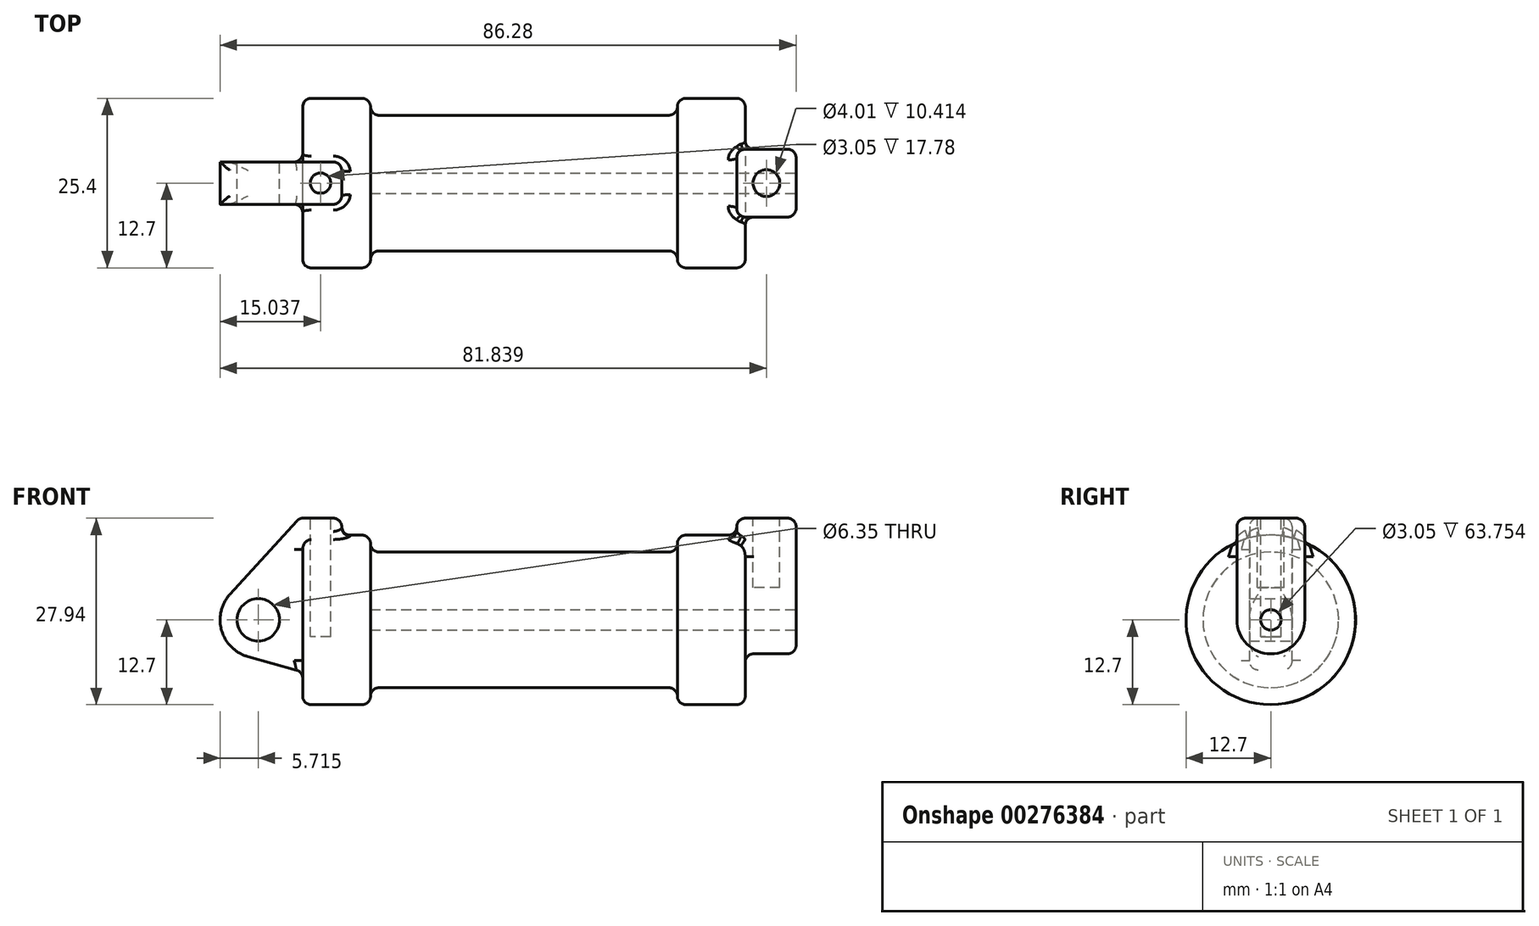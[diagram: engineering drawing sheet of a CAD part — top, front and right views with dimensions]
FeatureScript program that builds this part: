
annotation { "Feature Type Name" : "Feature", "Feature Type Description" : "" }
export const myFeature = defineFeature(function(context is Context, id is Id, definition is map)
    precondition{}
    {
        {
            var Q0;
            Q0=qCreatedBy(makeId("Front.planeOp"),FACE);
            var sketch = newSketch(context, id + "F0", { "sketchPlane" : qUnion([Q0])});
            skLineSegment(sketch, "E0", {"start": v(0, 0) * mm, "end": v(0, 12.7) * mm});
            skLineSegment(sketch, "E1", {"start": v(0, 12.7) * mm, "end": v(10.16, 12.7) * mm});
            skLineSegment(sketch, "E2", {"start": v(10.16, 12.7) * mm, "end": v(10.16, 10.16) * mm});
            skLineSegment(sketch, "E3", {"start": v(10.16, 10.16) * mm, "end": v(56.13, 10.16) * mm});
            skLineSegment(sketch, "E4", {"start": v(56.13, 10.16) * mm, "end": v(56.13, 12.7) * mm});
            skLineSegment(sketch, "E5", {"start": v(56.13, 12.7) * mm, "end": v(66.3, 12.7) * mm});
            skLineSegment(sketch, "E6", {"start": v(66.3, 12.7) * mm, "end": v(66.3, 0) * mm});
            skLineSegment(sketch, "E7", {"start": v(66.3, 0) * mm, "end": v(0, 0) * mm});
            skLineSegment(sketch, "E8", {"start": v(5.84, 15.24) * mm, "end": v(-0.5, 15.24) * mm});
            skLineSegment(sketch, "E9", {"start": v(-0.5, 15.24) * mm, "end": v(-10.88, 3.85) * mm});
            skLineSegment(sketch, "E10", {"start": v(0, 0) * mm, "end": v(-6.65, 0) * mm});
            skArc(sketch, "E11", {"start": v(-10.88, 3.85) * mm, "mid": v(-12.15, -1.58) * mm, "end": v(-8.18, -5.5) * mm});
            skCircle(sketch, "E12", {"center": v(-6.65, 0) * mm, "radius": 3.18 * mm});
            skLineSegment(sketch, "E13", {"start": v(5.84, 15.24) * mm, "end": v(5.84, -9.4) * mm});
            skLineSegment(sketch, "E14", {"start": v(5.84, -9.4) * mm, "end": v(-8.18, -5.5) * mm});
            skSolve(sketch);
        }
        {
            var Q0;
            {var subQ0=sQuery(id+"F0.wireOp",EDGE,"E2");Q0=makeQuery(id+"F0.imprint","IMPRINT",FACE,{"disambiguationData":[TD([[makeQuery(id+"F0.imprint","IMPRINT",EDGE,{"derivedFrom":subQ0}),-1.0]])]});}
            var Q1;
            {var subQ0=sQuery(id+"F0.wireOp",EDGE,"E0");Q1=makeQuery(id+"F0.imprint","IMPRINT",FACE,{"disambiguationData":[TD([[makeQuery(id+"F0.imprint","IMPRINT",EDGE,{"derivedFrom":subQ0}),-1.0]])]});}
            var Q2;
            Q2=sQuery(id+"F0.wireOp",EDGE,"E7");
            revolve(context, id + "F1", {"entities" : qUnion([Q0, Q1]), "axis" : qUnion([Q2]), "revolveType" : RevolveType.FULL});
        }
        {
            var Q0;
            {var subQ3=sQuery(id+"F0.wireOp",EDGE,"E0");Q0=makeQuery(id+"F0.imprint","IMPRINT",FACE,{"disambiguationData":[TD([[makeQuery(id+"F0.imprint","IMPRINT",EDGE,{"derivedFrom":subQ3}),1.0]])]});}
            var sketch = newSketch(context, id + "F2", { "sketchPlane" : qUnion([Q0])});
            skSolve(sketch);
        }
        {
            var Q0;
            {var subQ3=sQuery(id+"F0.wireOp",EDGE,"E0");Q0=makeQuery(id+"F2.imprint","IMPRINT",FACE,{"disambiguationData":[TD([[makeQuery(id+"F2.imprint","IMPRINT",EDGE,{"derivedFrom":makeQuery(id+"F0.imprint","IMPRINT",EDGE,{"derivedFrom":subQ3})}),1.0]])]});}
            var sketch = newSketch(context, id + "F3", { "sketchPlane" : qUnion([Q0])});
            skSolve(sketch);
        }
        {
            var Q0;
            Q0 = qSketchRegion(id + "F3", true);
            var Q1;
            {var subQ3=sQuery(id+"F0.wireOp",EDGE,"E0");Q1=makeQuery(id+"F2.imprint","IMPRINT",FACE,{"disambiguationData":[TD([[makeQuery(id+"F2.imprint","IMPRINT",EDGE,{"derivedFrom":makeQuery(id+"F0.imprint","IMPRINT",EDGE,{"derivedFrom":subQ3})}),1.0]])]});}
            extrude(context, id + "F4", {"entities" : qUnion([Q0, Q1]), "endBound" : BoundingType.SYMMETRIC, "depth" : 6.35 * mm});
        }
        {
            var Q0;
            Q0=makeQuery(id+"F1.opRevolve","SWEPT_FACE",FACE,{"disambiguationData":[OSD([sQuery(id+"F0.wireOp",EDGE,"E6")])]});
            var sketch = newSketch(context, id + "F5", { "sketchPlane" : qUnion([Q0])});
            skCircle(sketch, "E15", {"center": v(0, 0) * mm, "radius": 5.08 * mm});
            skCircle(sketch, "E16", {"center": v(0, 0) * mm, "radius": 1.52 * mm});
            skLineSegment(sketch, "E17", {"start": v(-5.08, 0) * mm, "end": v(-5.08, 15.24) * mm});
            skLineSegment(sketch, "E18", {"start": v(-5.08, 15.24) * mm, "end": v(5.08, 15.24) * mm});
            skLineSegment(sketch, "E19", {"start": v(5.08, 0) * mm, "end": v(5.08, 15.24) * mm});
            skSolve(sketch);
        }
        {
            var Q0;
            Q0 = qSketchRegion(id + "F5", true);
            extrude(context, id + "F6", {"entities" : qUnion([Q0]), "oppositeDirection" : true, "depth" : 1.27 * mm});
        }
        {
            var Q0;
            Q0=makeQuery(id+"F6.opExtrude","CAP_FACE",FACE,{"disambiguationData":[OSD([sQuery(id+"F5.wireOp",EDGE,"E15"),sQuery(id+"F5.wireOp",EDGE,"E16"),sQuery(id+"F5.wireOp",EDGE,"E17"),sQuery(id+"F5.wireOp",EDGE,"E18"),sQuery(id+"F5.wireOp",EDGE,"E19")])],"isStart":true});
            extrude(context, id + "F7", {"entities" : qUnion([Q0]), "operationType" : NewBodyOperationType.ADD, "depth" : 7.62 * mm});
        }
        {
            var Q0;
            Q0=makeQuery(id+"F4.opExtrude","SWEPT_FACE",FACE,{"disambiguationData":[OSD([sQuery(id+"F0.wireOp",EDGE,"E8")])]});
            var sketch = newSketch(context, id + "F8", { "sketchPlane" : qUnion([Q0])});
            skLineSegment(sketch, "E20", {"start": v(2.67, 3.18) * mm, "end": v(2.67, -3.18) * mm});
            skCircle(sketch, "E21", {"center": v(2.67, 0) * mm, "radius": 1.52 * mm});
            skSolve(sketch);
        }
        {
            var Q0;
            Q0 = qSketchRegion(id + "F8", true);
            extrude(context, id + "F9", {"entities" : qUnion([Q0]), "operationType" : NewBodyOperationType.REMOVE, "oppositeDirection" : true, "depth" : 17.78 * mm});
        }
        {
            var Q0;
            {var subQ0=sQuery(id+"F5.wireOp",EDGE,"E18");Q0=makeQuery(id+"F7.boolean.opBoolean","MERGE",FACE,{"derivedFrom":[makeQuery(id+"F6.opExtrude","SWEPT_FACE",FACE,{"disambiguationData":[OSD([subQ0])]}),makeQuery(id+"F7.opExtrude","SWEPT_FACE",FACE,{"disambiguationData":[OSD([subQ0])]})]});}
            var sketch = newSketch(context, id + "F10", { "sketchPlane" : qUnion([Q0])});
            skLineSegment(sketch, "E22", {"start": v(65.02, 0) * mm, "end": v(73.91, 0) * mm});
            skCircle(sketch, "E23", {"center": v(69.47, 0) * mm, "radius": 2 * mm});
            skSolve(sketch);
        }
        {
            var Q0;
            Q0 = qSketchRegion(id + "F10", true);
            extrude(context, id + "F11", {"entities" : qUnion([Q0]), "operationType" : NewBodyOperationType.REMOVE, "oppositeDirection" : true, "depth" : 10.4 * mm});
        }
        {
            var Q0;
            {var subQ0=sQuery(id+"F5.wireOp",EDGE,"E16");Q0=makeQuery(id+"F7.boolean.opBoolean","SPLIT",FACE,{"disambiguationData":[TD([makeQuery(id+"F6.opExtrude","SWEPT_FACE",FACE,{"disambiguationData":[OSD([subQ0])]})])],"derivedFrom":makeQuery(id+"F1.opRevolve","SWEPT_FACE",FACE,{"disambiguationData":[OSD([sQuery(id+"F0.wireOp",EDGE,"E6")])]})});}
            var sketch = newSketch(context, id + "F12", { "sketchPlane" : qUnion([Q0])});
            skCircle(sketch, "E24", {"center": v(0, 0) * mm, "radius": 1.52 * mm});
            skSolve(sketch);
        }
        {
            var Q0;
            Q0 = qSketchRegion(id + "F12", true);
            var Q1;
            Q1=makeQuery(id+"F1.opRevolve","SWEPT_FACE",FACE,{"disambiguationData":[OSD([sQuery(id+"F0.wireOp",EDGE,"E2")])]});
            extrude(context, id + "F13", {"entities" : qUnion([Q0]), "operationType" : NewBodyOperationType.REMOVE, "endBound" : BoundingType.UP_TO_SURFACE, "oppositeDirection" : true, "endBoundEntityFace" : qUnion([Q1]), "depth" : 25.4 * mm});
        }
        {
            var Q0;
            {var subQ0=sQuery(id+"F5.wireOp",EDGE,"E19");var subQ1=sQuery(id+"F5.wireOp",EDGE,"E18");Q0=makeQuery(id+"F7.boolean.opBoolean","MERGE",EDGE,{"derivedFrom":[makeQuery(id+"F6.opExtrude","SWEPT_EDGE",EDGE,{"disambiguationData":[OSD([subQ1,subQ0])]}),makeQuery(id+"F7.opExtrude","SWEPT_EDGE",EDGE,{"disambiguationData":[OSD([subQ1,subQ0])]})]});}
            var Q1;
            Q1=makeQuery(id+"F7.opExtrude","CAP_EDGE",EDGE,{"disambiguationData":[OSD([sQuery(id+"F5.wireOp",EDGE,"E19")])],"isStart":false});
            var Q2;
            Q2=makeQuery(id+"F7.opExtrude","CAP_EDGE",EDGE,{"disambiguationData":[OSD([sQuery(id+"F5.wireOp",EDGE,"E18")])],"isStart":false});
            var Q3;
            Q3=makeQuery(id+"F7.opExtrude","CAP_EDGE",EDGE,{"disambiguationData":[OSD([sQuery(id+"F5.wireOp",EDGE,"E17")])],"isStart":false});
            var Q4;
            Q4=makeQuery(id+"F7.opExtrude","CAP_EDGE",EDGE,{"disambiguationData":[OSD([sQuery(id+"F5.wireOp",EDGE,"E15")])],"isStart":false});
            var Q5;
            Q5=makeQuery(id+"F1.opRevolve","SWEPT_EDGE",EDGE,{"disambiguationData":[OSD([sQuery(id+"F0.wireOp",EDGE,"E5"),sQuery(id+"F0.wireOp",EDGE,"E6")])]});
            var Q6;
            Q6=makeQuery(id+"F1.opRevolve","SWEPT_EDGE",EDGE,{"disambiguationData":[OSD([sQuery(id+"F0.wireOp",EDGE,"E4"),sQuery(id+"F0.wireOp",EDGE,"E5")])]});
            var Q7;
            Q7=makeQuery(id+"F6.opExtrude","CAP_EDGE",EDGE,{"disambiguationData":[OSD([sQuery(id+"F5.wireOp",EDGE,"E18")])],"isStart":false});
            var Q8;
            {var subQ0=sQuery(id+"F5.wireOp",EDGE,"E18");var subQ1=sQuery(id+"F5.wireOp",EDGE,"E17");Q8=makeQuery(id+"F7.boolean.opBoolean","MERGE",EDGE,{"derivedFrom":[makeQuery(id+"F6.opExtrude","SWEPT_EDGE",EDGE,{"disambiguationData":[OSD([subQ1,subQ0])]}),makeQuery(id+"F7.opExtrude","SWEPT_EDGE",EDGE,{"disambiguationData":[OSD([subQ1,subQ0])]})]});}
            var Q9;
            Q9=makeQuery(id+"F4.opExtrude","CAP_EDGE",EDGE,{"disambiguationData":[OSD([sQuery(id+"F0.wireOp",EDGE,"E8")])],"isStart":true});
            var Q10;
            Q10=makeQuery(id+"F1.opRevolve","SWEPT_EDGE",EDGE,{"disambiguationData":[OSD([sQuery(id+"F0.wireOp",EDGE,"E1"),sQuery(id+"F0.wireOp",EDGE,"E2")])]});
            var Q11;
            Q11=makeQuery(id+"F1.opRevolve","SWEPT_EDGE",EDGE,{"disambiguationData":[OSD([sQuery(id+"F0.wireOp",EDGE,"E0"),sQuery(id+"F0.wireOp",EDGE,"E1")])]});
            var Q12;
            Q12=makeQuery(id+"F4.opExtrude","CAP_EDGE",EDGE,{"disambiguationData":[OSD([sQuery(id+"F0.wireOp",EDGE,"E9")])],"isStart":true});
            var Q13;
            Q13=makeQuery(id+"F4.opExtrude","CAP_EDGE",EDGE,{"disambiguationData":[OSD([sQuery(id+"F0.wireOp",EDGE,"E9")])],"isStart":false});
            var Q14;
            Q14=makeQuery(id+"F4.opExtrude","CAP_EDGE",EDGE,{"disambiguationData":[OSD([sQuery(id+"F0.wireOp",EDGE,"E8")])],"isStart":false});
            var Q15;
            Q15=makeQuery(id+"F4.opExtrude","SWEPT_EDGE",EDGE,{"disambiguationData":[OSD([sQuery(id+"F0.wireOp",EDGE,"E8"),sQuery(id+"F0.wireOp",EDGE,"E13")])]});
            var Q16;
            Q16=makeQuery(id+"F4.opExtrude","SWEPT_EDGE",EDGE,{"disambiguationData":[OSD([sQuery(id+"F0.wireOp",EDGE,"E8"),sQuery(id+"F0.wireOp",EDGE,"E9")])]});
            var Q17;
            Q17=makeQuery(id+"F4.opExtrude","CAP_EDGE",EDGE,{"disambiguationData":[OSD([sQuery(id+"F0.wireOp",EDGE,"E11")])],"isStart":true});
            var Q18;
            Q18=makeQuery(id+"F4.opExtrude","CAP_EDGE",EDGE,{"disambiguationData":[OSD([sQuery(id+"F0.wireOp",EDGE,"E14")])],"isStart":true});
            var Q19;
            Q19=makeQuery(id+"F4.opExtrude","CAP_EDGE",EDGE,{"disambiguationData":[OSD([sQuery(id+"F0.wireOp",EDGE,"E11")])],"isStart":false});
            var Q20;
            Q20=makeQuery(id+"F4.opExtrude","CAP_EDGE",EDGE,{"disambiguationData":[OSD([sQuery(id+"F0.wireOp",EDGE,"E14")])],"isStart":false});
            fillet(context, id + "F14", {"entities" : qUnion([Q0, Q1, Q2, Q3, Q4, Q5, Q6, Q7, Q8, Q9, Q10, Q11, Q12, Q13, Q14, Q15, Q16, Q17, Q18, Q19, Q20]), "radius" : 1.27 * mm, "allowEdgeOverflow" : false});
        }
        {
            var Q0;
            Q0=makeQuery(id+"F7.boolean.opBoolean","INTERSECT",EDGE,{"derivedFrom":[makeQuery(id+"F1.opRevolve","SWEPT_FACE",FACE,{"disambiguationData":[OSD([sQuery(id+"F0.wireOp",EDGE,"E6")])]}),makeQuery(id+"F7.opExtrude","SWEPT_FACE",FACE,{"disambiguationData":[OSD([sQuery(id+"F5.wireOp",EDGE,"E17")])]})]});
            var Q1;
            Q1=makeQuery(id+"F7.boolean.opBoolean","INTERSECT",EDGE,{"derivedFrom":[makeQuery(id+"F1.opRevolve","SWEPT_FACE",FACE,{"disambiguationData":[OSD([sQuery(id+"F0.wireOp",EDGE,"E5")])]}),makeQuery(id+"F6.opExtrude","CAP_FACE",FACE,{"disambiguationData":[OSD([sQuery(id+"F5.wireOp",EDGE,"E15"),sQuery(id+"F5.wireOp",EDGE,"E16"),sQuery(id+"F5.wireOp",EDGE,"E17"),sQuery(id+"F5.wireOp",EDGE,"E18"),sQuery(id+"F5.wireOp",EDGE,"E19")])],"isStart":false})]});
            var Q2;
            Q2=makeQuery(id+"F6.opExtrude","CAP_EDGE",EDGE,{"disambiguationData":[OSD([sQuery(id+"F5.wireOp",EDGE,"E17")])],"isStart":false});
            var Q3;
            Q3=makeQuery(id+"F6.opExtrude","CAP_EDGE",EDGE,{"disambiguationData":[OSD([sQuery(id+"F5.wireOp",EDGE,"E19")])],"isStart":false});
            fillet(context, id + "F15", {"entities" : qUnion([Q0, Q1, Q2, Q3]), "radius" : 1.27 * mm, "tangentPropagation" : true, "allowEdgeOverflow" : false});
        }
        {
            var Q0;
            Q0=makeQuery(id+"F1.opRevolve","SWEPT_EDGE",EDGE,{"disambiguationData":[OSD([sQuery(id+"F0.wireOp",EDGE,"E3"),sQuery(id+"F0.wireOp",EDGE,"E4")])]});
            var Q1;
            Q1=makeQuery(id+"F1.opRevolve","SWEPT_EDGE",EDGE,{"disambiguationData":[OSD([sQuery(id+"F0.wireOp",EDGE,"E2"),sQuery(id+"F0.wireOp",EDGE,"E3")])]});
            var Q2;
            Q2=makeQuery(id+"F7.boolean.opBoolean","INTERSECT",EDGE,{"derivedFrom":[makeQuery(id+"F1.opRevolve","SWEPT_FACE",FACE,{"disambiguationData":[OSD([sQuery(id+"F0.wireOp",EDGE,"E6")])]}),makeQuery(id+"F7.opExtrude","SWEPT_FACE",FACE,{"disambiguationData":[OSD([sQuery(id+"F5.wireOp",EDGE,"E19")])]})]});
            var Q3;
            Q3=makeQuery(id+"F7.boolean.opBoolean","INTERSECT",EDGE,{"derivedFrom":[makeQuery(id+"F1.opRevolve","SWEPT_FACE",FACE,{"disambiguationData":[OSD([sQuery(id+"F0.wireOp",EDGE,"E6")])]}),makeQuery(id+"F7.opExtrude","SWEPT_FACE",FACE,{"disambiguationData":[OSD([sQuery(id+"F5.wireOp",EDGE,"E15")])]})]});
            var Q4;
            Q4=makeQuery(id+"F7.boolean.opBoolean","INTERSECT",EDGE,{"derivedFrom":[makeQuery(id+"F1.opRevolve","SWEPT_FACE",FACE,{"disambiguationData":[OSD([sQuery(id+"F0.wireOp",EDGE,"E5")])]}),makeQuery(id+"F6.opExtrude","CAP_FACE",FACE,{"disambiguationData":[OSD([sQuery(id+"F5.wireOp",EDGE,"E15"),sQuery(id+"F5.wireOp",EDGE,"E16"),sQuery(id+"F5.wireOp",EDGE,"E17"),sQuery(id+"F5.wireOp",EDGE,"E18"),sQuery(id+"F5.wireOp",EDGE,"E19")])],"isStart":false})]});
            fillet(context, id + "F16", {"entities" : qUnion([Q0, Q1, Q2, Q3, Q4]), "radius" : 1.27 * mm, "tangentPropagation" : true, "allowEdgeOverflow" : false});
        }
        {
            var Q0;
            {var subQ0=sQuery(id+"F0.wireOp",EDGE,"E8");Q0=makeQuery(id+"F15.opFillet","BLEND_EDGE",EDGE,{"blendedFrom":[makeQuery(id+"F4.opExtrude","SWEPT_EDGE",EDGE,{"disambiguationData":[OSD([subQ0,sQuery(id+"F0.wireOp",EDGE,"E13")])]}),makeQuery(id+"F4.opExtrude","CAP_EDGE",EDGE,{"disambiguationData":[OSD([subQ0])],"isStart":false})],"blendedInto":[]});}
            var Q1;
            {var subQ0=sQuery(id+"F0.wireOp",EDGE,"E13");Q1=makeQuery(id+"F4.opExtrude","CAP_EDGE",EDGE,{"disambiguationData":[OSD([subQ0]),TDD([makeQuery(id+"F2.imprint","IMPRINT",EDGE,{"derivedFrom":makeQuery(id+"F0.imprint","IMPRINT",EDGE,{"disambiguationData":[TD([[makeQuery(id+"F0.imprint","INTERSECT",VERTEX,{"derivedFrom":[sQuery(id+"F0.wireOp",EDGE,"E8"),subQ0]}),-1.0]])],"derivedFrom":subQ0})})])],"isStart":false});}
            var Q2;
            {var subQ0=sQuery(id+"F0.wireOp",EDGE,"E8");Q2=makeQuery(id+"F15.opFillet","BLEND_EDGE",EDGE,{"blendedFrom":[makeQuery(id+"F4.opExtrude","SWEPT_EDGE",EDGE,{"disambiguationData":[OSD([subQ0,sQuery(id+"F0.wireOp",EDGE,"E13")])]}),makeQuery(id+"F4.opExtrude","CAP_EDGE",EDGE,{"disambiguationData":[OSD([subQ0])],"isStart":true})],"blendedInto":[]});}
            fillet(context, id + "F17", {"entities" : qUnion([Q0, Q1, Q2]), "radius" : 1.27 * mm, "tangentPropagation" : true, "allowEdgeOverflow" : false});
        }
        {
            var Q0;
            Q0=makeQuery(id+"F4.opExtrude","SWEPT_FACE",FACE,{"disambiguationData":[OSD([sQuery(id+"F0.wireOp",EDGE,"E1")])]});
            extrude(context, id + "F18", {"entities" : qUnion([Q0]), "operationType" : NewBodyOperationType.ADD, "depth" : 0.5 * mm});
        }
        {
            var Q0;
            {var subQ0=sQuery(id+"F0.wireOp",EDGE,"E1");Q0=makeQuery(id+"F18.boolean.opBoolean","INTERSECT",EDGE,{"derivedFrom":[makeQuery(id+"F1.opRevolve","SWEPT_FACE",FACE,{"disambiguationData":[OSD([subQ0])]}),makeQuery(id+"F18.opExtrude","SWEPT_FACE",FACE,{"disambiguationData":[OSD([subQ0]),TDD([makeQuery(id+"F4.opExtrude","CAP_EDGE",EDGE,{"disambiguationData":[OSD([subQ0])],"isStart":false})])]})]});}
            var Q1;
            {var subQ0=sQuery(id+"F0.wireOp",EDGE,"E1");Q1=makeQuery(id+"F18.boolean.opBoolean","INTERSECT",EDGE,{"derivedFrom":[makeQuery(id+"F1.opRevolve","SWEPT_FACE",FACE,{"disambiguationData":[OSD([sQuery(id+"F0.wireOp",EDGE,"E0")])]}),makeQuery(id+"F18.opExtrude","SWEPT_FACE",FACE,{"disambiguationData":[OSD([subQ0]),TDD([makeQuery(id+"F4.opExtrude","CAP_EDGE",EDGE,{"disambiguationData":[OSD([subQ0])],"isStart":false})])]})]});}
            fillet(context, id + "F19", {"entities" : qUnion([Q0, Q1]), "radius" : 1.27 * mm, "tangentPropagation" : true, "allowEdgeOverflow" : false});
        }
        {
            var Q0;
            {var subQ0=sQuery(id+"F0.wireOp",EDGE,"E1");Q0=makeQuery(id+"F18.boolean.opBoolean","INTERSECT",EDGE,{"derivedFrom":[makeQuery(id+"F1.opRevolve","SWEPT_FACE",FACE,{"disambiguationData":[OSD([subQ0])]}),makeQuery(id+"F18.opExtrude","SWEPT_FACE",FACE,{"disambiguationData":[OSD([subQ0]),TDD([makeQuery(id+"F4.opExtrude","CAP_EDGE",EDGE,{"disambiguationData":[OSD([subQ0])],"isStart":true})])]})]});}
            var Q1;
            {var subQ0=sQuery(id+"F0.wireOp",EDGE,"E13");var subQ1=sQuery(id+"F0.wireOp",EDGE,"E1");Q1=makeQuery(id+"F18.boolean.opBoolean","MERGE",EDGE,{"derivedFrom":[makeQuery(id+"F4.opExtrude","CAP_EDGE",EDGE,{"disambiguationData":[OSD([subQ0]),TDD([makeQuery(id+"F2.imprint","IMPRINT",EDGE,{"derivedFrom":makeQuery(id+"F0.imprint","IMPRINT",EDGE,{"disambiguationData":[TD([[makeQuery(id+"F0.imprint","INTERSECT",VERTEX,{"derivedFrom":[sQuery(id+"F0.wireOp",EDGE,"E8"),subQ0]}),-1.0]])],"derivedFrom":subQ0})})])],"isStart":true}),makeQuery(id+"F18.opExtrude","SWEPT_EDGE",EDGE,{"disambiguationData":[OSD([subQ1,subQ0]),TDD([makeQuery(id+"F4.opExtrude","CAP_VERTEX",VERTEX,{"disambiguationData":[OSD([subQ1,subQ0])],"isStart":true})])]})]});}
            fillet(context, id + "F20", {"entities" : qUnion([Q0, Q1]), "radius" : 1.27 * mm, "tangentPropagation" : true, "allowEdgeOverflow" : false});
        }
    });
